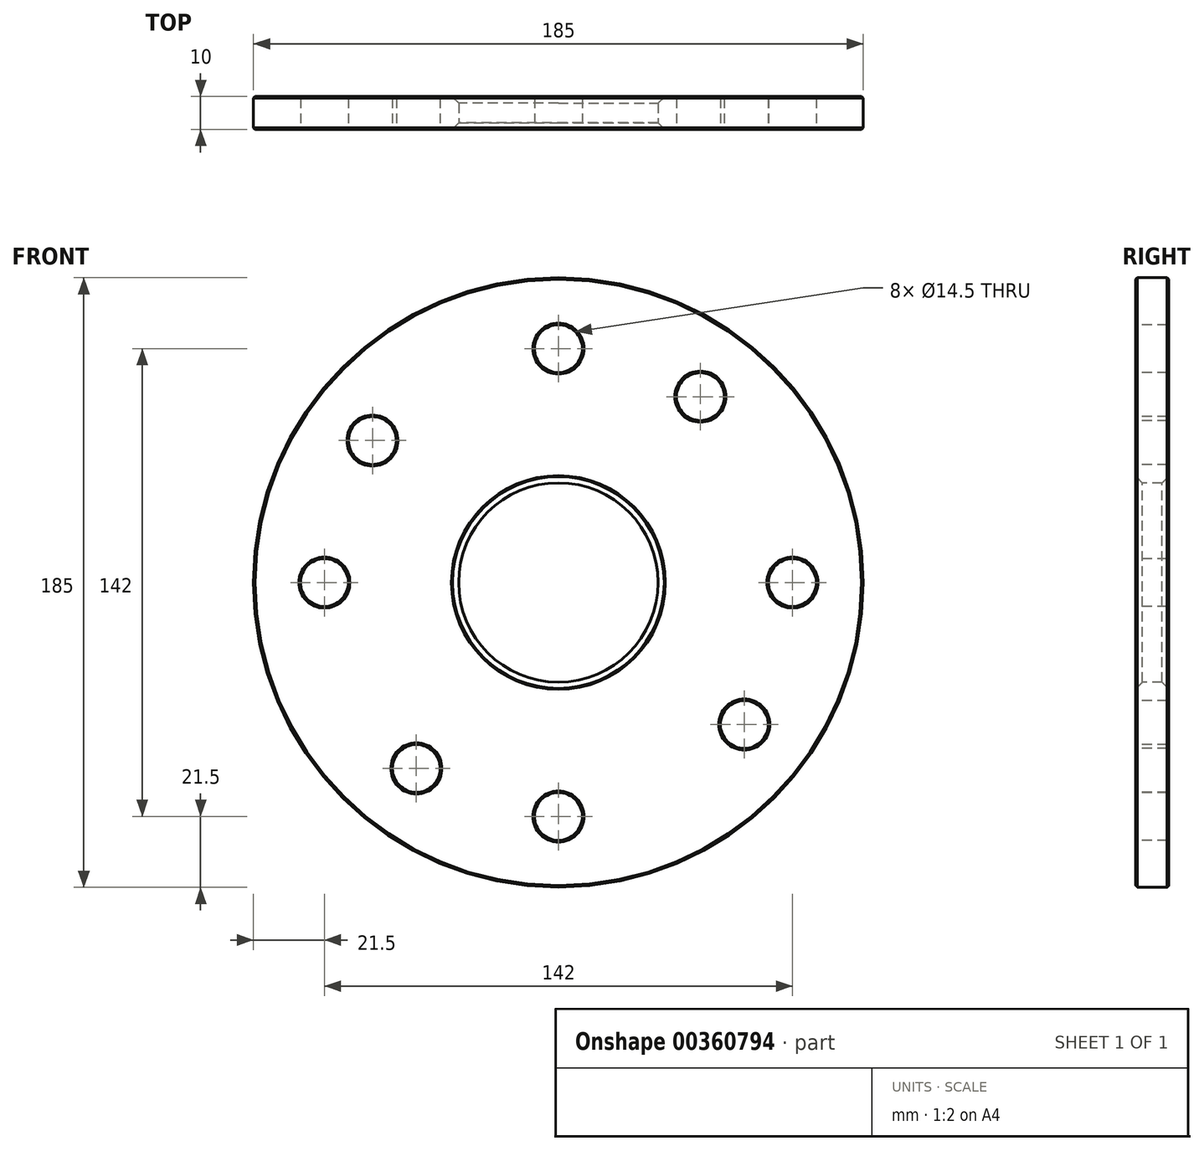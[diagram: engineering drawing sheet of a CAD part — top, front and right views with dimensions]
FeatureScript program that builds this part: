
annotation { "Feature Type Name" : "Feature", "Feature Type Description" : "" }
export const myFeature = defineFeature(function(context is Context, id is Id, definition is map)
    precondition{}
    {
        {
            var Q0;
            Q0=qCreatedBy(makeId("Front.planeOp"),FACE);
            var sketch = newSketch(context, id + "F0", { "sketchPlane" : qUnion([Q0])});
            skCircle(sketch, "E0", {"center": v(0, 0) * mm, "radius": 92.5 * mm});
            skCircle(sketch, "E1", {"center": v(0, 71) * mm, "radius": 7.25 * mm});
            skCircle(sketch, "E2.1.0", {"center": v(-71, 0) * mm, "radius": 7.25 * mm});
            skCircle(sketch, "E2.2.0", {"center": v(0, -71) * mm, "radius": 7.25 * mm});
            skCircle(sketch, "E2.3.0", {"center": v(71, 0) * mm, "radius": 7.25 * mm});
            skCircle(sketch, "E3", {"center": v(-43.1, -56.42) * mm, "radius": 7.25 * mm});
            skLineSegment(sketch, "E4", {"start": v(-43.1, -56.42) * mm, "end": v(0, -71) * mm});
            skCircle(sketch, "E5.1.0", {"center": v(56.42, -43.1) * mm, "radius": 7.25 * mm});
            skCircle(sketch, "E5.2.0", {"center": v(43.1, 56.42) * mm, "radius": 7.25 * mm});
            skCircle(sketch, "E6.1.3.0", {"center": v(-56.42, 43.1) * mm, "radius": 7.25 * mm});
            skCircle(sketch, "E7", {"center": v(0, 0) * mm, "radius": 30.25 * mm});
            skSolve(sketch);
        }
        {
            var Q0;
            Q0=makeQuery(id+"F0.imprint","IMPRINT",FACE,{"disambiguationData":[TD([[makeQuery(id+"F0.imprint","IMPRINT",EDGE,{"derivedFrom":sQuery(id+"F0.wireOp",EDGE,"E0")}),1.0]])]});
            extrude(context, id + "F1", {"entities" : qUnion([Q0]), "oppositeDirection" : true, "depth" : 10 * mm});
        }
        {
            var Q0;
            Q0=makeQuery(id+"F1.opExtrude","CAP_EDGE",EDGE,{"disambiguationData":[OSD([sQuery(id+"F0.wireOp",EDGE,"E7")])],"isStart":true});
            chamfer(context, id + "F2", {"entities" : qUnion([Q0]), "chamferType" : ChamferType.OFFSET_ANGLE, "width" : 2 * mm, "oppositeDirection" : true, "angle" : 45 * degree, "tangentPropagation" : true});
        }
        {
            var Q0;
            Q0=makeQuery(id+"F1.opExtrude","CAP_EDGE",EDGE,{"disambiguationData":[OSD([sQuery(id+"F0.wireOp",EDGE,"E7")])],"isStart":false});
            chamfer(context, id + "F3", {"entities" : qUnion([Q0]), "chamferType" : ChamferType.OFFSET_ANGLE, "width" : 2 * mm, "oppositeDirection" : false, "angle" : 45 * degree, "tangentPropagation" : true});
        }
        {
            var Q0;
            Q0=makeQuery(id+"F1.opExtrude","CAP_FACE",FACE,{"disambiguationData":[OSD([sQuery(id+"F0.wireOp",EDGE,"E0"),sQuery(id+"F0.wireOp",EDGE,"E1"),sQuery(id+"F0.wireOp",EDGE,"E2.1.0"),sQuery(id+"F0.wireOp",EDGE,"E2.2.0"),sQuery(id+"F0.wireOp",EDGE,"E2.3.0"),sQuery(id+"F0.wireOp",EDGE,"E3"),sQuery(id+"F0.wireOp",EDGE,"E5.1.0"),sQuery(id+"F0.wireOp",EDGE,"E5.2.0"),sQuery(id+"F0.wireOp",EDGE,"E6.1.3.0"),sQuery(id+"F0.wireOp",EDGE,"E7")])],"isStart":false});
            chamfer(context, id + "F4", {"entities" : qUnion([Q0]), "chamferType" : ChamferType.OFFSET_ANGLE, "width" : 0.5 * mm, "oppositeDirection" : false, "angle" : 45 * degree, "tangentPropagation" : true});
        }
        {
            var Q0;
            Q0=makeQuery(id+"F1.opExtrude","CAP_FACE",FACE,{"disambiguationData":[OSD([sQuery(id+"F0.wireOp",EDGE,"E0"),sQuery(id+"F0.wireOp",EDGE,"E1"),sQuery(id+"F0.wireOp",EDGE,"E2.1.0"),sQuery(id+"F0.wireOp",EDGE,"E2.2.0"),sQuery(id+"F0.wireOp",EDGE,"E2.3.0"),sQuery(id+"F0.wireOp",EDGE,"E3"),sQuery(id+"F0.wireOp",EDGE,"E5.1.0"),sQuery(id+"F0.wireOp",EDGE,"E5.2.0"),sQuery(id+"F0.wireOp",EDGE,"E6.1.3.0"),sQuery(id+"F0.wireOp",EDGE,"E7")])],"isStart":true});
            chamfer(context, id + "F5", {"entities" : qUnion([Q0]), "width" : 0.5 * mm, "tangentPropagation" : true});
        }
    });
